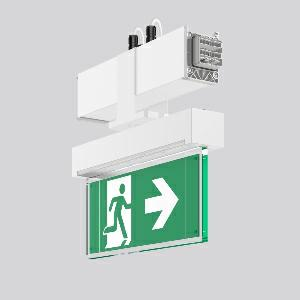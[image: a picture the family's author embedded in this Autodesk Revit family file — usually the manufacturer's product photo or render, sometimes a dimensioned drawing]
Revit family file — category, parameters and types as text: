
# Revit family: linedo_module_rz_9503rz_762_434_023_261c
name_source: partatom
category: Lighting Fixtures
units: mm (PartAtom-declared; Revit-internal decimal feet)

## family parameters
Cut with Voids When Loaded = No
Host = Face
Light Source = No
Part Type = Normal
Room Calculation Point = No
Round Connector Dimension = Use Diameter
Shared = No

## types (1)
- LINEDO Module RZ
    Apparent Load = 0 VA
    Default Elevation = 1800 mm
    Description = LINEDO, white, on/off
Continuous line luminaire, L 336 B 62 H 308, SBS, 3 h, MultiDigit
    Height = 308 mm
    Lamp = 0 x
    Length = 336 mm
    Luminous efficacy = 0 lm/W
    Manufacturer = RZB
    ModVariant = No
    Model = 9503RZ.762.434.023
    Mounting Place = Ceiling
    Mounting Type = Surface mounted
    Number of Poles = 1
    OnlyDefault = Yes
    Power Factor = 1
    Product Name = LINEDO Module RZ
    Product group = Surface mounted continuous line luminaire system
    ProductGroupID = 310
    Protection Class = Protection class I
    Protection Degree = IP 54
    RLX_Detail_Level = 1
    RLX_Emergency_Light_Flux = 0 lm
    RLX_Emergency_Type = 0
    RLX_Emergency_Type_DB = No
    RlxData = <blob elided: 33145 chars, md5=0ca7bf4f>
    Standby Power = 0 W
    System Light Flux = 0 lm
    System Power = 0 W
    Type Comments = Product without accessories
    Type Image = 9503rz.762.434.023.jpg
    URL = http://relux.com
    VarID = ---
    Voltage = 0 V
    Weight = 0.00 kg
    Width = 62 mm  [stored 0.203412 ft]

note: [stored X ft] marks values corroborated as IEEE doubles in the binary element streams (Revit-internal decimal feet)

## geometry (parser evidence)
native form markers: Blend x4, Sweep x12
no freeform markers — native parametric forms only
